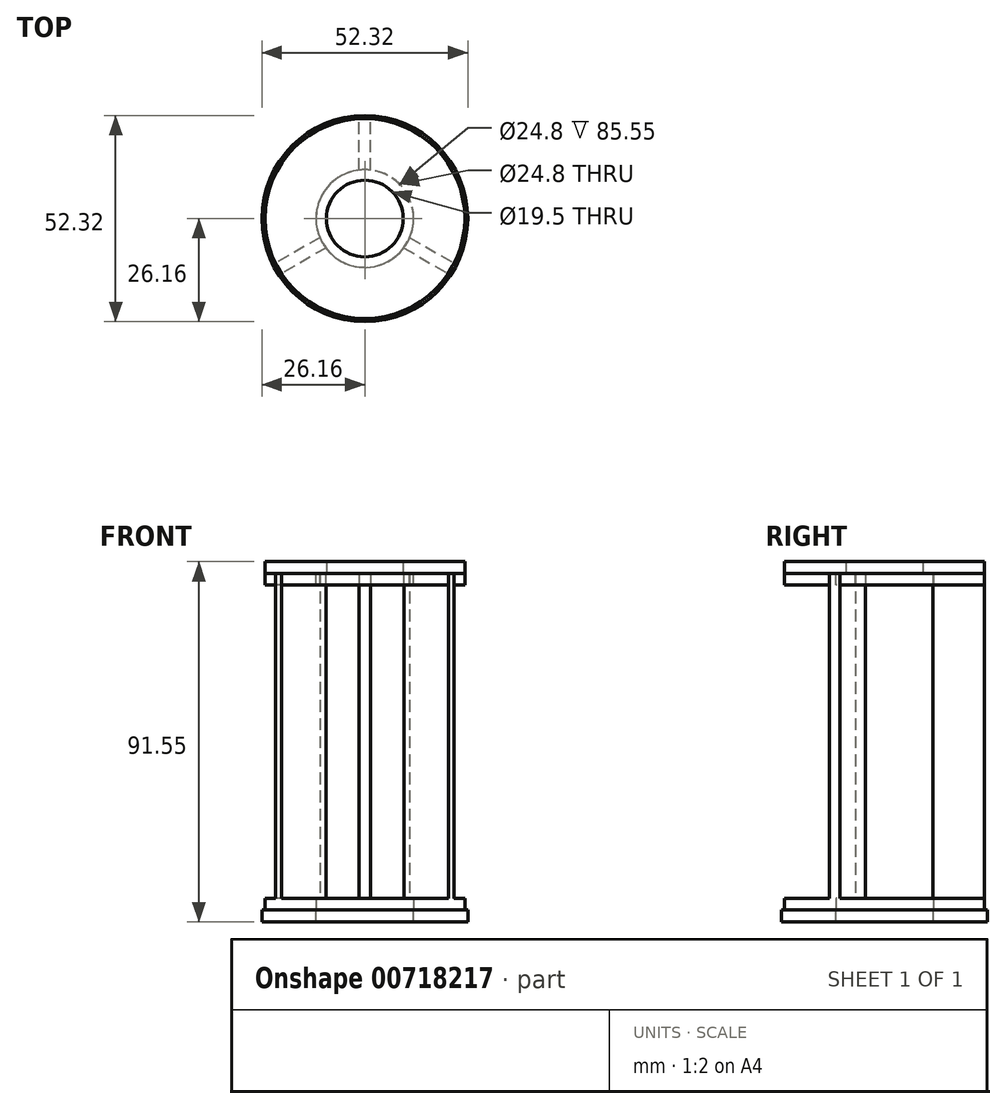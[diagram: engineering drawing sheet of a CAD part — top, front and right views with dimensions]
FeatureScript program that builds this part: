
annotation { "Feature Type Name" : "Feature", "Feature Type Description" : "" }
export const myFeature = defineFeature(function(context is Context, id is Id, definition is map)
    precondition{}
    {
        {
            var Q0;
            Q0=qCreatedBy(makeId("Top.planeOp"),FACE);
            var sketch = newSketch(context, id + "F0", { "sketchPlane" : qUnion([Q0])});
            skCircle(sketch, "E0", {"center": v(0, 0) * mm, "radius": 12.4 * mm});
            skCircle(sketch, "E1", {"center": v(0, 0) * mm, "radius": 26.16 * mm});
            skCircle(sketch, "E2", {"center": v(0, 0) * mm, "radius": 25.4 * mm});
            skSolve(sketch);
        }
        {
            var Q0;
            Q0=qSketchRegion(id+"F0",true);
            var Q1;
            Q1=makeQuery(id+"F0.imprint","IMPRINT",FACE,{"disambiguationData":[TD([[makeQuery(id+"F0.imprint","IMPRINT",EDGE,{"derivedFrom":sQuery(id+"F0.wireOp",EDGE,"E0")}),-1.0]])]});
            extrude(context, id + "F1", {"entities" : qUnion([Q0, Q1]), "oppositeDirection" : true, "depth" : 3 * mm});
        }
        {
            var Q0;
            Q0=makeQuery(id+"F0.imprint","IMPRINT",FACE,{"disambiguationData":[TD([[makeQuery(id+"F0.imprint","IMPRINT",EDGE,{"derivedFrom":sQuery(id+"F0.wireOp",EDGE,"E0")}),-1.0]])]});
            extrude(context, id + "F2", {"entities" : qUnion([Q0]), "depth" : 3 * mm});
        }
        {
            var Q0;
            Q0=makeQuery(id+"F2.opExtrude","CAP_FACE",FACE,{"disambiguationData":[OSD([sQuery(id+"F0.wireOp",EDGE,"E0"),sQuery(id+"F0.wireOp",EDGE,"E2")])],"isStart":false});
            var sketch = newSketch(context, id + "F3", { "sketchPlane" : qUnion([Q0])});
            skLineSegment(sketch, "E3", {"start": v(0, 12.4) * mm, "end": v(0, 25.4) * mm, "construction": true});
            skLineSegment(sketch, "E4", {"start": v(1.5, 12.3) * mm, "end": v(1.5, 25.36) * mm});
            skLineSegment(sketch, "E5.MirrorCS", {"start": v(-1.5, 12.3) * mm, "end": v(-1.5, 25.36) * mm});
            skLineSegment(sketch, "E6.1.0", {"start": v(-9.9, -7.45) * mm, "end": v(-21.2, -13.98) * mm});
            skLineSegment(sketch, "E6.1.1", {"start": v(-11.4, -4.86) * mm, "end": v(-22.7, -11.38) * mm});
            skLineSegment(sketch, "E6.2.0", {"start": v(11.4, -4.86) * mm, "end": v(22.7, -11.38) * mm});
            skLineSegment(sketch, "E6.2.1", {"start": v(9.9, -7.45) * mm, "end": v(21.2, -13.98) * mm});
            skSolve(sketch);
        }
        {
            var Q0;
            {var subQ0=sQuery(id+"F3.wireOp",EDGE,"E6.2.0");Q0=makeQuery(id+"F3.imprint","IMPRINT",FACE,{"disambiguationData":[TD([[makeQuery(id+"F3.imprint","IMPRINT",EDGE,{"derivedFrom":subQ0}),-1.0]])]});}
            var Q1;
            {var subQ0=sQuery(id+"F3.wireOp",EDGE,"E6.1.0");Q1=makeQuery(id+"F3.imprint","IMPRINT",FACE,{"disambiguationData":[TD([[makeQuery(id+"F3.imprint","IMPRINT",EDGE,{"derivedFrom":subQ0}),-1.0]])]});}
            var Q2;
            {var subQ0=sQuery(id+"F3.wireOp",EDGE,"E4");Q2=makeQuery(id+"F3.imprint","IMPRINT",FACE,{"disambiguationData":[TD([[makeQuery(id+"F3.imprint","IMPRINT",EDGE,{"derivedFrom":subQ0}),1.0]])]});}
            extrude(context, id + "F4", {"entities" : qUnion([Q0, Q1, Q2]), "operationType" : NewBodyOperationType.ADD, "depth" : 82.55 * mm});
        }
        {
            var Q0;
            Q0=makeQuery(id+"F4.opExtrude","CAP_FACE",FACE,{"disambiguationData":[OSD([sQuery(id+"F0.wireOp",EDGE,"E0"),sQuery(id+"F0.wireOp",EDGE,"E2"),sQuery(id+"F3.wireOp",EDGE,"E4"),sQuery(id+"F3.wireOp",EDGE,"E5.MirrorCS")])],"isStart":false});
            var sketch = newSketch(context, id + "F5", { "sketchPlane" : qUnion([Q0])});
            skCircle(sketch, "E7.0", {"center": v(0, 0) * mm, "radius": 25.4 * mm});
            skCircle(sketch, "E8", {"center": v(0, 0) * mm, "radius": 9.75 * mm});
            skCircle(sketch, "E9.0", {"center": v(0, 0) * mm, "radius": 12.4 * mm});
            skLineSegment(sketch, "E10.0", {"start": v(9.9, -7.45) * mm, "end": v(21.2, -13.98) * mm});
            skLineSegment(sketch, "E11.0", {"start": v(11.4, -4.86) * mm, "end": v(22.7, -11.38) * mm});
            skLineSegment(sketch, "E12.0", {"start": v(-9.9, -7.45) * mm, "end": v(-21.2, -13.98) * mm});
            skLineSegment(sketch, "E13.0", {"start": v(-11.4, -4.86) * mm, "end": v(-22.7, -11.38) * mm});
            skLineSegment(sketch, "E14.0", {"start": v(-1.5, 12.3) * mm, "end": v(-1.5, 25.36) * mm});
            skLineSegment(sketch, "E15.0", {"start": v(1.5, 12.3) * mm, "end": v(1.5, 25.36) * mm});
            skSolve(sketch);
        }
        {
            var Q0;
            Q0=makeQuery(id+"F5.imprint","IMPRINT",FACE,{"disambiguationData":[TD([[makeQuery(id+"F5.imprint","IMPRINT",EDGE,{"derivedFrom":sQuery(id+"F5.wireOp",EDGE,"E8")}),-1.0]])]});
            var Q1;
            {var subQ1=sQuery(id+"F3.wireOp",EDGE,"E4");var subQ2=makeQuery(id+"F4.opExtrude","CAP_EDGE",EDGE,{"disambiguationData":[OSD([subQ1])],"isStart":false});Q1=makeQuery(id+"F5.imprint","IMPRINT",FACE,{"disambiguationData":[TD([[makeQuery(id+"F5.imprint","IMPRINT",EDGE,{"derivedFrom":subQ2}),1.0]])]});}
            var Q2;
            {var subQ0=sQuery(id+"F5.wireOp",EDGE,"E10.0");Q2=makeQuery(id+"F5.imprint","IMPRINT",FACE,{"disambiguationData":[TD([[makeQuery(id+"F5.imprint","IMPRINT",EDGE,{"derivedFrom":subQ0}),-1.0]])]});}
            var Q3;
            {var subQ2=sQuery(id+"F5.wireOp",EDGE,"E11.0");Q3=makeQuery(id+"F5.imprint","IMPRINT",FACE,{"disambiguationData":[TD([[makeQuery(id+"F5.imprint","IMPRINT",EDGE,{"derivedFrom":subQ2}),1.0]])]});}
            var Q4;
            {var subQ0=sQuery(id+"F5.wireOp",EDGE,"E10.0");Q4=makeQuery(id+"F5.imprint","IMPRINT",FACE,{"disambiguationData":[TD([[makeQuery(id+"F5.imprint","IMPRINT",EDGE,{"derivedFrom":subQ0}),1.0]])]});}
            var Q5;
            {var subQ2=sQuery(id+"F5.wireOp",EDGE,"E13.0");Q5=makeQuery(id+"F5.imprint","IMPRINT",FACE,{"disambiguationData":[TD([[makeQuery(id+"F5.imprint","IMPRINT",EDGE,{"derivedFrom":subQ2}),-1.0]])]});}
            var Q6;
            {var subQ0=sQuery(id+"F5.wireOp",EDGE,"E12.0");Q6=makeQuery(id+"F5.imprint","IMPRINT",FACE,{"disambiguationData":[TD([[makeQuery(id+"F5.imprint","IMPRINT",EDGE,{"derivedFrom":subQ0}),-1.0]])]});}
            var Q7;
            {var subQ2=sQuery(id+"F5.wireOp",EDGE,"E14.0");Q7=makeQuery(id+"F5.imprint","IMPRINT",FACE,{"disambiguationData":[TD([[makeQuery(id+"F5.imprint","IMPRINT",EDGE,{"derivedFrom":subQ2}),-1.0]])]});}
            extrude(context, id + "F6", {"entities" : qUnion([Q0, Q1, Q2, Q3, Q4, Q5, Q6, Q7]), "depth" : 3 * mm});
        }
        {
            var Q0;
            {var subQ2=sQuery(id+"F5.wireOp",EDGE,"E11.0");Q0=makeQuery(id+"F5.imprint","IMPRINT",FACE,{"disambiguationData":[TD([[makeQuery(id+"F5.imprint","IMPRINT",EDGE,{"derivedFrom":subQ2}),1.0]])]});}
            var Q1;
            {var subQ2=sQuery(id+"F5.wireOp",EDGE,"E13.0");Q1=makeQuery(id+"F5.imprint","IMPRINT",FACE,{"disambiguationData":[TD([[makeQuery(id+"F5.imprint","IMPRINT",EDGE,{"derivedFrom":subQ2}),-1.0]])]});}
            var Q2;
            {var subQ0=sQuery(id+"F5.wireOp",EDGE,"E10.0");Q2=makeQuery(id+"F5.imprint","IMPRINT",FACE,{"disambiguationData":[TD([[makeQuery(id+"F5.imprint","IMPRINT",EDGE,{"derivedFrom":subQ0}),-1.0]])]});}
            extrude(context, id + "F7", {"entities" : qUnion([Q0, Q1, Q2]), "oppositeDirection" : true, "depth" : 3 * mm});
        }
    });
